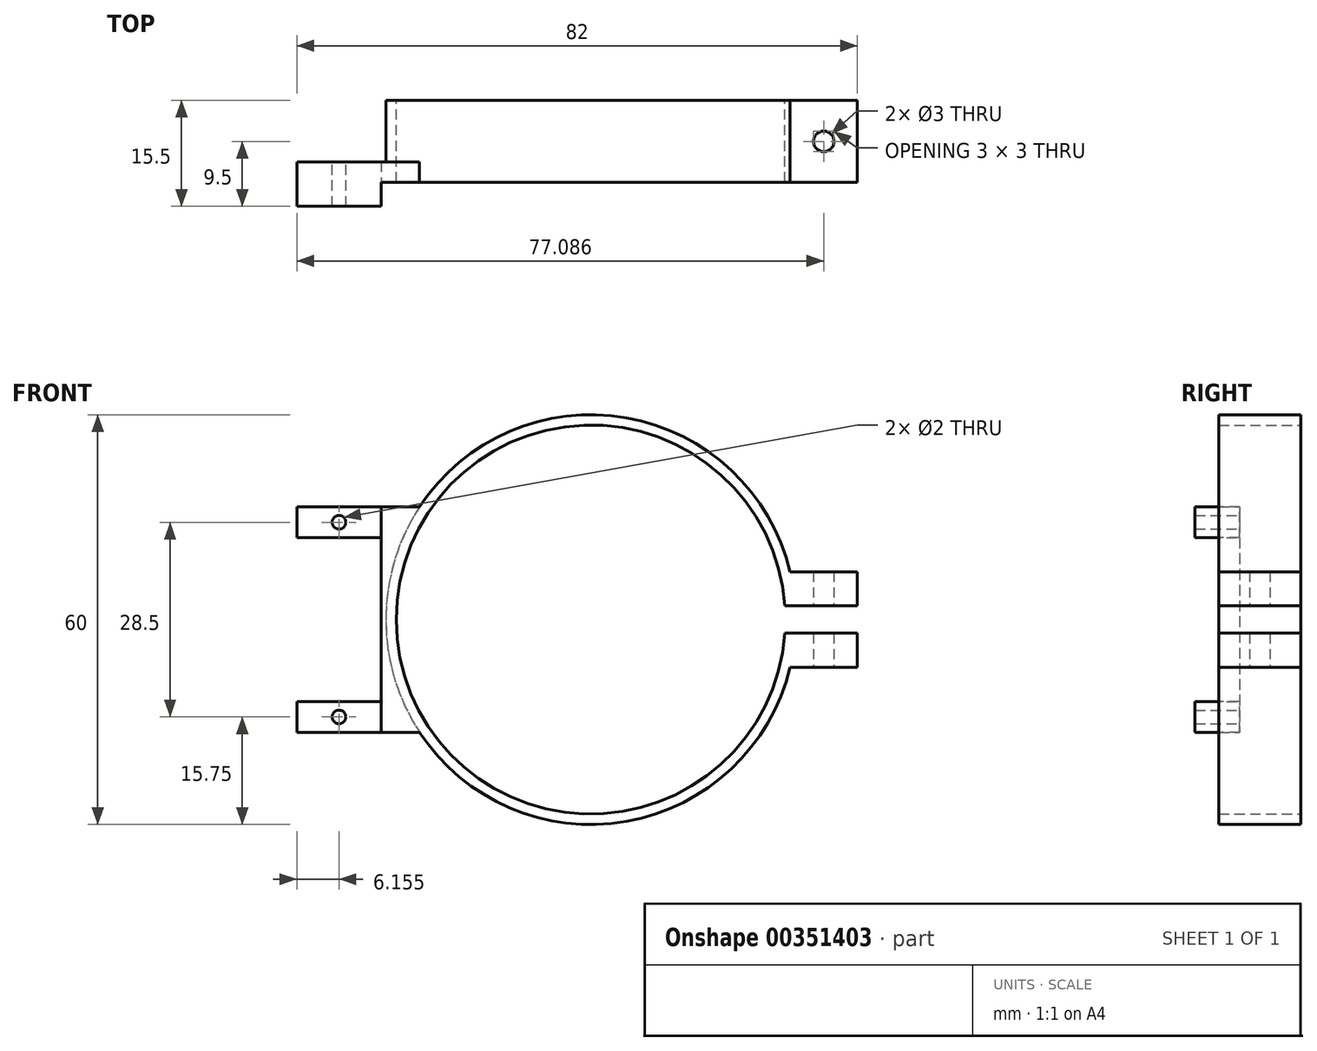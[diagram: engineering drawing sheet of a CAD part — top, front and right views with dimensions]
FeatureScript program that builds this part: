
annotation { "Feature Type Name" : "Feature", "Feature Type Description" : "" }
export const myFeature = defineFeature(function(context is Context, id is Id, definition is map)
    precondition{}
    {
        {
            var Q0;
            Q0=qCreatedBy(makeId("Front.planeOp"),FACE);
            var sketch = newSketch(context, id + "F0", { "sketchPlane" : qUnion([Q0])});
            skCircle(sketch, "E0", {"center": v(0, 0) * mm, "radius": 28.48 * mm});
            skCircle(sketch, "E1", {"center": v(0, 0) * mm, "radius": 30 * mm});
            skLineSegment(sketch, "E2", {"start": v(30, 0) * mm, "end": v(39, 0) * mm});
            skLineSegment(sketch, "E3", {"start": v(39, 0) * mm, "end": v(39, -7) * mm});
            skLineSegment(sketch, "E4", {"start": v(39, -7) * mm, "end": v(29.17, -7) * mm});
            skLineSegment(sketch, "E5", {"start": v(39, 0) * mm, "end": v(39, 7) * mm});
            skLineSegment(sketch, "E6", {"start": v(39, 7) * mm, "end": v(29.17, 7) * mm});
            skSolve(sketch);
        }
        {
            var Q0;
            Q0 = qSketchRegion(id + "F0", true);
            extrude(context, id + "F1", {"entities" : qUnion([Q0]), "depth" : 12 * mm});
        }
        {
            var Q0;
            Q0=makeQuery(id+"F1.opExtrude","CAP_FACE",FACE,{"disambiguationData":[OSD([sQuery(id+"F0.wireOp",EDGE,"E0"),sQuery(id+"F0.wireOp",EDGE,"E1"),sQuery(id+"F0.wireOp",EDGE,"E3"),sQuery(id+"F0.wireOp",EDGE,"E4"),sQuery(id+"F0.wireOp",EDGE,"E5"),sQuery(id+"F0.wireOp",EDGE,"E6")])],"isStart":false});
            var sketch = newSketch(context, id + "F2", { "sketchPlane" : qUnion([Q0])});
            skLineSegment(sketch, "E7.bottom", {"start": v(44.15, 2) * mm, "end": v(24.16, 2) * mm});
            skLineSegment(sketch, "E7.top", {"start": v(44.15, -2) * mm, "end": v(24.16, -2) * mm});
            skLineSegment(sketch, "E7.left", {"start": v(44.15, 2) * mm, "end": v(44.15, -2) * mm});
            skLineSegment(sketch, "E7.right", {"start": v(24.16, 2) * mm, "end": v(24.16, -2) * mm});
            skPoint(sketch, "E7.middle", {"position": v(34.16, 0) * mm});
            skSolve(sketch);
        }
        {
            var Q0;
            Q0 = qSketchRegion(id + "F2", true);
            extrude(context, id + "F3", {"entities" : qUnion([Q0]), "operationType" : NewBodyOperationType.REMOVE, "oppositeDirection" : true, "depth" : 25 * mm});
        }
        {
            var Q0;
            Q0=makeQuery(id+"F1.opExtrude","SWEPT_FACE",FACE,{"disambiguationData":[OSD([sQuery(id+"F0.wireOp",EDGE,"E4")])]});
            var sketch = newSketch(context, id + "F4", { "sketchPlane" : qUnion([Q0])});
            skLineSegment(sketch, "E8", {"start": v(39, 12) * mm, "end": v(39, 0) * mm, "construction": true});
            skLineSegment(sketch, "E9", {"start": v(39, 0) * mm, "end": v(29.17, 0) * mm, "construction": true});
            skLineSegment(sketch, "E10", {"start": v(29.17, 0) * mm, "end": v(29.17, 12) * mm, "construction": true});
            skLineSegment(sketch, "E11", {"start": v(29.17, 12) * mm, "end": v(39, 12) * mm, "construction": true});
            skLineSegment(sketch, "E12", {"start": v(39, 12) * mm, "end": v(29.17, 0) * mm, "construction": true});
            skLineSegment(sketch, "E13", {"start": v(29.17, 12) * mm, "end": v(39, 0) * mm, "construction": true});
            skCircle(sketch, "E14", {"center": v(34.09, 6) * mm, "radius": 1.5 * mm});
            skSolve(sketch);
        }
        {
            var Q0;
            Q0 = qSketchRegion(id + "F4", true);
            extrude(context, id + "F5", {"entities" : qUnion([Q0]), "operationType" : NewBodyOperationType.REMOVE, "oppositeDirection" : true, "depth" : 25 * mm});
        }
        {
            var Q0;
            Q0=makeQuery(id+"F1.opExtrude","CAP_FACE",FACE,{"disambiguationData":[OSD([sQuery(id+"F0.wireOp",EDGE,"E0"),sQuery(id+"F0.wireOp",EDGE,"E1"),sQuery(id+"F0.wireOp",EDGE,"E3"),sQuery(id+"F0.wireOp",EDGE,"E4"),sQuery(id+"F0.wireOp",EDGE,"E5"),sQuery(id+"F0.wireOp",EDGE,"E6")])],"isStart":false});
            var sketch = newSketch(context, id + "F6", { "sketchPlane" : qUnion([Q0])});
            skLineSegment(sketch, "E15", {"start": v(-30, 0) * mm, "end": v(-43, 0) * mm});
            skPoint(sketch, "E15.endSnap0", {"position": v(-30, 0) * mm});
            skLineSegment(sketch, "E16", {"start": v(-43, 0) * mm, "end": v(-43, 16.5) * mm});
            skLineSegment(sketch, "E17", {"start": v(-43, 16.5) * mm, "end": v(-25.05, 16.5) * mm});
            skLineSegment(sketch, "E18", {"start": v(-25.05, 16.5) * mm, "end": v(-43, 16.5) * mm});
            skLineSegment(sketch, "E19", {"start": v(-43, 0) * mm, "end": v(-43, -16.5) * mm});
            skLineSegment(sketch, "E20", {"start": v(-43, -16.5) * mm, "end": v(-25.05, -16.5) * mm});
            skLineSegment(sketch, "E21", {"start": v(-25.05, 16.5) * mm, "end": v(-23.2, 16.5) * mm});
            skLineSegment(sketch, "E22", {"start": v(-25.05, -16.5) * mm, "end": v(-23.2, -16.5) * mm});
            skArc(sketch, "E23", {"start": v(-23.2, 16.5) * mm, "mid": v(-28.6, 0) * mm, "end": v(-23.2, -16.5) * mm});
            skSolve(sketch);
        }
        {
            var Q0;
            Q0 = qSketchRegion(id + "F6", true);
            extrude(context, id + "F7", {"entities" : qUnion([Q0]), "operationType" : NewBodyOperationType.ADD, "oppositeDirection" : true, "depth" : 3 * mm});
        }
        {
            var Q0;
            Q0=makeQuery(id+"F7.boolean.opBoolean","MERGE",FACE,{"derivedFrom":[makeQuery(id+"F1.opExtrude","CAP_FACE",FACE,{"disambiguationData":[OSD([sQuery(id+"F0.wireOp",EDGE,"E0"),sQuery(id+"F0.wireOp",EDGE,"E1"),sQuery(id+"F0.wireOp",EDGE,"E3"),sQuery(id+"F0.wireOp",EDGE,"E4"),sQuery(id+"F0.wireOp",EDGE,"E5"),sQuery(id+"F0.wireOp",EDGE,"E6")])],"isStart":false}),makeQuery(id+"F7.opExtrude","CAP_FACE",FACE,{"disambiguationData":[OSD([sQuery(id+"F6.wireOp",EDGE,"E16"),sQuery(id+"F6.wireOp",EDGE,"E18"),sQuery(id+"F6.wireOp",EDGE,"E19"),sQuery(id+"F6.wireOp",EDGE,"E20"),sQuery(id+"F6.wireOp",EDGE,"E21"),sQuery(id+"F6.wireOp",EDGE,"E22"),sQuery(id+"F6.wireOp",EDGE,"E23")])],"isStart":true})]});
            var sketch = newSketch(context, id + "F8", { "sketchPlane" : qUnion([Q0])});
            skLineSegment(sketch, "E24.bottom", {"start": v(-43, 16.5) * mm, "end": v(-30.69, 16.5) * mm});
            skLineSegment(sketch, "E24.top", {"start": v(-43, 12) * mm, "end": v(-30.69, 12) * mm});
            skLineSegment(sketch, "E24.left", {"start": v(-43, 16.5) * mm, "end": v(-43, 12) * mm});
            skLineSegment(sketch, "E24.right", {"start": v(-30.69, 16.5) * mm, "end": v(-30.69, 12) * mm});
            skLineSegment(sketch, "E25.bottom", {"start": v(-43, -16.5) * mm, "end": v(-30.69, -16.5) * mm});
            skLineSegment(sketch, "E25.top", {"start": v(-43, -12) * mm, "end": v(-30.69, -12) * mm});
            skLineSegment(sketch, "E25.left", {"start": v(-43, -16.5) * mm, "end": v(-43, -12) * mm});
            skLineSegment(sketch, "E25.right", {"start": v(-30.69, -16.5) * mm, "end": v(-30.69, -12) * mm});
            skSolve(sketch);
        }
        {
            var Q0;
            Q0 = qSketchRegion(id + "F8", true);
            extrude(context, id + "F9", {"entities" : qUnion([Q0]), "operationType" : NewBodyOperationType.ADD, "depth" : 3.5 * mm});
        }
        {
            var Q0;
            Q0=makeQuery(id+"F7.boolean.opBoolean","MERGE",FACE,{"derivedFrom":[makeQuery(id+"F1.opExtrude","CAP_FACE",FACE,{"disambiguationData":[OSD([sQuery(id+"F0.wireOp",EDGE,"E0"),sQuery(id+"F0.wireOp",EDGE,"E1"),sQuery(id+"F0.wireOp",EDGE,"E3"),sQuery(id+"F0.wireOp",EDGE,"E4"),sQuery(id+"F0.wireOp",EDGE,"E5"),sQuery(id+"F0.wireOp",EDGE,"E6")])],"isStart":false}),makeQuery(id+"F7.opExtrude","CAP_FACE",FACE,{"disambiguationData":[OSD([sQuery(id+"F6.wireOp",EDGE,"E16"),sQuery(id+"F6.wireOp",EDGE,"E18"),sQuery(id+"F6.wireOp",EDGE,"E19"),sQuery(id+"F6.wireOp",EDGE,"E20"),sQuery(id+"F6.wireOp",EDGE,"E21"),sQuery(id+"F6.wireOp",EDGE,"E22"),sQuery(id+"F6.wireOp",EDGE,"E23")])],"isStart":true})]});
            var sketch = newSketch(context, id + "F10", { "sketchPlane" : qUnion([Q0])});
            skLineSegment(sketch, "E26.bottom", {"start": v(-43, 12) * mm, "end": v(-30.69, 12) * mm});
            skLineSegment(sketch, "E26.top", {"start": v(-43, -12) * mm, "end": v(-30.69, -12) * mm});
            skLineSegment(sketch, "E26.left", {"start": v(-43, 12) * mm, "end": v(-43, -12) * mm});
            skLineSegment(sketch, "E26.right", {"start": v(-30.69, 12) * mm, "end": v(-30.69, -12) * mm});
            skSolve(sketch);
        }
        {
            var Q0;
            Q0 = qSketchRegion(id + "F10", true);
            extrude(context, id + "F11", {"entities" : qUnion([Q0]), "operationType" : NewBodyOperationType.REMOVE, "oppositeDirection" : true, "depth" : 25 * mm});
        }
        {
            var Q0;
            Q0=makeQuery(id+"F7.opExtrude","CAP_FACE",FACE,{"disambiguationData":[OSD([sQuery(id+"F6.wireOp",EDGE,"E16"),sQuery(id+"F6.wireOp",EDGE,"E18"),sQuery(id+"F6.wireOp",EDGE,"E19"),sQuery(id+"F6.wireOp",EDGE,"E20"),sQuery(id+"F6.wireOp",EDGE,"E21"),sQuery(id+"F6.wireOp",EDGE,"E22"),sQuery(id+"F6.wireOp",EDGE,"E23")])],"isStart":false});
            var sketch = newSketch(context, id + "F12", { "sketchPlane" : qUnion([Q0])});
            skLineSegment(sketch, "E27", {"start": v(30.69, 12) * mm, "end": v(43, 16.5) * mm, "construction": true});
            skLineSegment(sketch, "E28", {"start": v(43, 16.5) * mm, "end": v(43, 12) * mm, "construction": true});
            skLineSegment(sketch, "E29", {"start": v(43, 12) * mm, "end": v(30.69, 16.5) * mm, "construction": true});
            skLineSegment(sketch, "E30", {"start": v(30.69, 16.5) * mm, "end": v(30.69, -16.5) * mm, "construction": true});
            skLineSegment(sketch, "E31", {"start": v(30.69, -16.5) * mm, "end": v(43, -12) * mm, "construction": true});
            skLineSegment(sketch, "E32", {"start": v(43, -12) * mm, "end": v(43, -16.5) * mm, "construction": true});
            skLineSegment(sketch, "E33", {"start": v(43, -16.5) * mm, "end": v(30.69, -12) * mm, "construction": true});
            skCircle(sketch, "E34", {"center": v(36.84, 14.25) * mm, "radius": 1 * mm});
            skCircle(sketch, "E35", {"center": v(36.84, -14.25) * mm, "radius": 1 * mm});
            skSolve(sketch);
        }
        {
            var Q0;
            Q0 = qSketchRegion(id + "F12", true);
            extrude(context, id + "F13", {"entities" : qUnion([Q0]), "operationType" : NewBodyOperationType.REMOVE, "oppositeDirection" : true, "depth" : 25 * mm});
        }
    });
